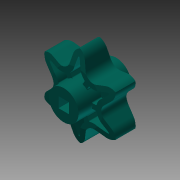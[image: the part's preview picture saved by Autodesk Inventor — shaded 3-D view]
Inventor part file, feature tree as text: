
AUTODESK INVENTOR PART (.ipt)
format: ipt  version: 2013 (Build 170138000, 138)  size: 550,912 bytes
history: native  units: in
note: dims shown in document units (in); Inventor stores cm internally (conversion verified against a paired STEP export)
features: sketch x6, extrude x5, mirror x3, revolve x1, pattern_circular x1, other x1
ambient origin geometry x8: Origin, YZ Plane, XZ Plane, XY Plane, X Axis, Y Axis, Z Axis, Center Point
bodies: Solid1 (feature_tree)
feature tree (17):
  sketch  "Sketch1"  dims[d0=0.3in d1=0.0in d2=0.354in]
  extrude  "Extrusion1"  Depth=0.354in
  extrude  "Extrusion2"  Depth=0.163in TaperAngle=0.0deg
  mirror  "Mirror1"
  extrude  "Extrusion3"  Depth=0.032in
  sketch  "Sketch3"  dims[d8=0.602in d9=0.032in]
  revolve  "Revolution1"  [1 undecoded]
  mirror  "Mirror2"
  extrude  "Extrusion4"  Depth=2.3622in TaperAngle=360.0deg
  pattern_circular  "Circular Pattern1"  [2 undecoded]
  mirror  "Mirror3"
  sketch  "Sketch2"  dims[d3=0.163in d4=0.0in d6=0.163in d7=0.0in]
  sketch  "Sketch4"  dims[d10=90.0deg d11=0.111in d12=0.0in]
  sketch  "Sketch5"  dims[d13=0.354in d14=2.3622in d15=360.0deg]
  sketch  "Sketch6"  dims[d17=0.6875in d18=0.0in d19=0.0in d20=0.0in]
  other  "Srf1"
  extrude  "ExtrusionSrf1"  TaperAngle=0.0deg  [1 undecoded]
note: 4 required parameter values undecoded (feature->parameter linkage not recoverable at this tier; creation-order binding heuristic only, values carry confidence <= 0.55)